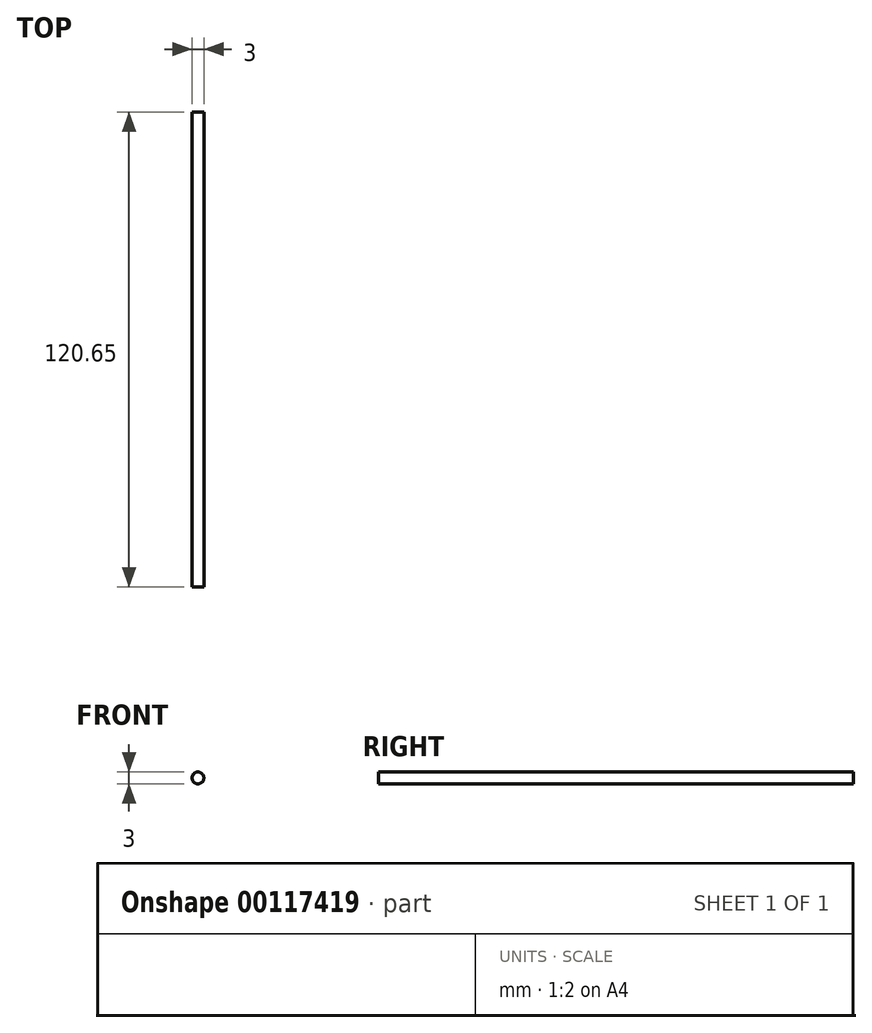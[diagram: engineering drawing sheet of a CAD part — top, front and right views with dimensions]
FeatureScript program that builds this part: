
annotation { "Feature Type Name" : "Feature", "Feature Type Description" : "" }
export const myFeature = defineFeature(function(context is Context, id is Id, definition is map)
    precondition{}
    {
        {
            var Q0;
            Q0=qCreatedBy(makeId("Front.planeOp"),FACE);
            var sketch = newSketch(context, id + "F0", { "sketchPlane" : qUnion([Q0])});
            skCircle(sketch, "E0", {"center": v(18.68, 12.5) * mm, "radius": 1.5 * mm});
            skSolve(sketch);
        }
        {
            var Q0;
            Q0=makeQuery(id+"F0.imprint","IMPRINT",FACE,{"disambiguationData":[TD([[makeQuery(id+"F0.imprint","IMPRINT",EDGE,{"derivedFrom":sQuery(id+"F0.wireOp",EDGE,"E0")}),1.0]])]});
            extrude(context, id + "F1", {"entities" : qUnion([Q0]), "depth" : 120.65 * mm});
        }
    });
